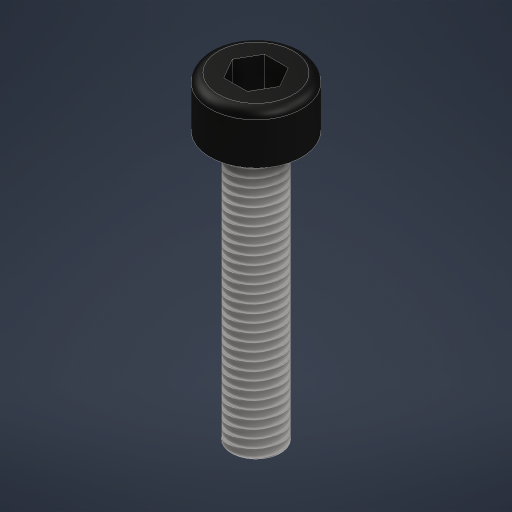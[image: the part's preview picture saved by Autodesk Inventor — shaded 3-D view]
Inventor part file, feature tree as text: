
AUTODESK INVENTOR PART (.ipt)
format: ipt  version: 2024 (Build 280153000, 153)  size: 246,784 bytes
history: native  units: mm
features: extrude x3, sketch x1, fillet x1, thread x1
ambient origin geometry x8: Origin, YZ Plane, XZ Plane, XY Plane, X Axis, Y Axis, Z Axis, Center Point
bodies: Solid1 (feature_tree)
feature tree (6):
  sketch  "Sketch1"  dims[d0=2.93mm d1=5.5mm d2=3.0mm d3=0.0mm d4=16.0mm d5=0.0mm d8=2.45mm d9=2.0mm d10=0.0mm d11=0.5mm d12=16.0mm d13=0.0mm]
  extrude  "Extrusion1"  Depth=16.0mm
  extrude  "Extrusion2"  Depth=3.0mm TaperAngle=0.0deg
  extrude  "Extrusion3"  Depth=16.0mm
  fillet  "Fillet1"  [1 undecoded]
  thread  "Thread2"  [1 undecoded]
note: 2 required parameter values undecoded (feature->parameter linkage not recoverable at this tier; creation-order binding heuristic only, values carry confidence <= 0.55)
